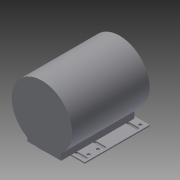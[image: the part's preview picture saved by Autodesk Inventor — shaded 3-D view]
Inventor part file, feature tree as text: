
AUTODESK INVENTOR PART (.ipt)
format: ipt  version: 2015 SP1 (Build 190203100, 203)  size: 212,480 bytes
history: native  units: in
note: dims shown in document units (in); Inventor stores cm internally (conversion verified against a paired STEP export)
features: sketch x7, extrude x5, plane x3, hole x1, projected_geometry x1
ambient origin geometry x8: Origin, YZ Plane, XZ Plane, XY Plane, X Axis, Y Axis, Z Axis, Center Point
bodies: Solid1 (feature_tree)
feature tree (17):
  extrude  "Extrusion1"  Depth=0.1in
  extrude  "Extrusion2"  Depth=2.0in
  hole  "Hole1"  [1 undecoded]
  plane  "Work Plane2"
  extrude  "Extrusion3"  TaperAngle=0.0deg  [1 undecoded]
  plane  "Work Plane7"
  extrude  "Extrusion4"  TaperAngle=45.0deg  [1 undecoded]
  plane  "Work Plane9"
  extrude  "Extrusion5"  TaperAngle=135.0deg  [1 undecoded]
  sketch  "Sketch7"  dims[d12=135.0deg d13=0.196in d14=0.5in d15=0.375in d16=0.25in d17=0.5635in d18=0.75in d19=0.8108in d20=7.877in d21=0.25in d22=3.65in d23=1.0in d24=0.0in d27=0.206in d28=0.0in d29=0.125in d30=0.0in d31=0.333in d38=0.333in d39=0.333in d40=0.902in d41=0.333in d51=0.3365in d52=0.25in d53=0.0in d54=7.0in d55=6.5in d56=2.003in d57=0.503in d58=0.266in d59=0.503in d60=3.564in d62=0.367in]
  sketch  "Sketch1"  dims[d0=0.625in d1=0.1in]
  sketch  "Sketch2"  dims[d2=0.191in d3=2.0in]
  sketch  "Sketch3"  dims[d4=0.0in d5=6.5in]
  sketch  "Sketch4"  dims[d6=8.377in d7=0.0in]
  projected_geometry  "Projected Loop1"
  sketch  "Sketch5"  dims[d8=5.75in d9=45.0deg]
  sketch  "Sketch6"  dims[d10=45.0deg d11=135.0deg]
note: 4 required parameter values undecoded (feature->parameter linkage not recoverable at this tier; creation-order binding heuristic only, values carry confidence <= 0.55)
